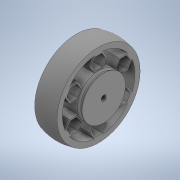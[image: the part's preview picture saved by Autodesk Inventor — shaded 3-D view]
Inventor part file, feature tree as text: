
AUTODESK INVENTOR PART (.ipt)
format: ipt  version: 2020 (Build 240168000, 168)  size: 317,952 bytes
history: native  units: in
note: dims shown in document units (in); Inventor stores cm internally (conversion verified against a paired STEP export)
features: sketch x4, extrude x2, revolve x2, projected_geometry x1
ambient origin geometry x8: Origin, YZ Plane, XZ Plane, XY Plane, X Axis, Y Axis, Z Axis, Center Point
bodies: Solid1 (feature_tree)
feature tree (9):
  extrude  "Extrusion1"  Depth=0.1181in
  sketch  "Sketch3"  dims[d6=0.9843in d7=0.1181in]
  revolve  "Revolution1"  [1 undecoded]
  extrude  "Extrusion2"  Depth=0.1181in
  revolve  "Revolution2"  [1 undecoded]
  sketch  "Sketch1"  dims[d0=0.1181in d1=0.0394in]
  sketch  "Sketch2"  dims[d3=1.8898in d4=0.1181in]
  projected_geometry  "Projected Loop1"
  sketch  "Sketch4"  dims[d8=0.0in d9=1.8898in d10=0.1181in d11=0.0315in d12=2.3622in d14=360.0deg d16=0.5118in d17=0.0in d19=90.0deg d20=0.0394in d22=45.0deg d24=0.0394in d25=90.0deg d26=45.0deg]
note: 2 required parameter values undecoded (feature->parameter linkage not recoverable at this tier; creation-order binding heuristic only, values carry confidence <= 0.55)
